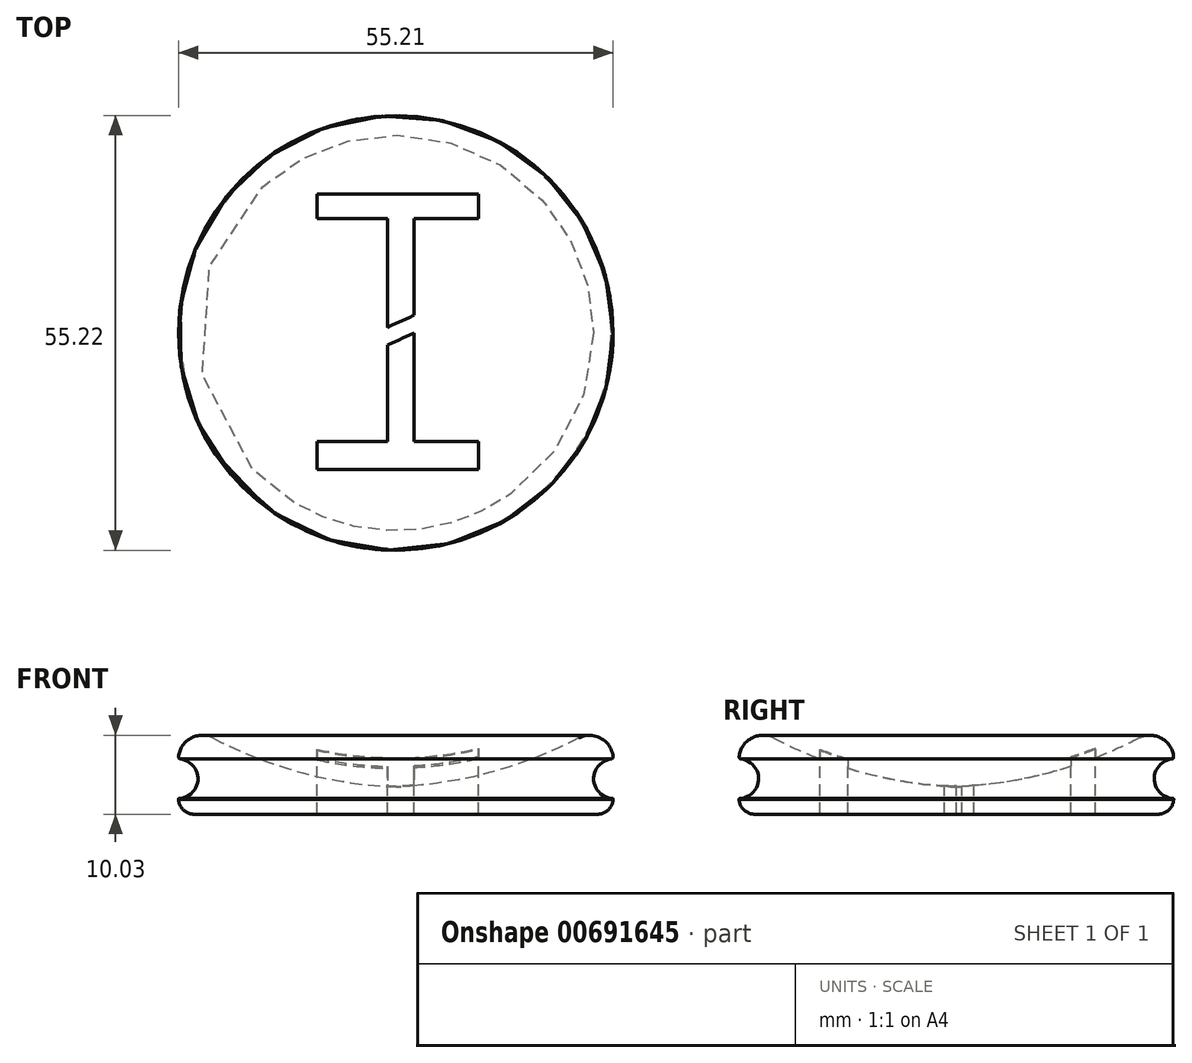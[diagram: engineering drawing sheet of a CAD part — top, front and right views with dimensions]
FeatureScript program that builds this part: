
annotation { "Feature Type Name" : "Feature", "Feature Type Description" : "" }
export const myFeature = defineFeature(function(context is Context, id is Id, definition is map)
    precondition{}
    {
        {
            var Q0;
            Q0=qCreatedBy(makeId("Front.planeOp"),FACE);
            var sketch = newSketch(context, id + "F0", { "sketchPlane" : qUnion([Q0])});
            skLineSegment(sketch, "E0.bottom", {"start": v(-25.5, -12.76) * mm, "end": v(-25, -12.76) * mm});
            skLineSegment(sketch, "E0.right", {"start": v(-25, -12.76) * mm, "end": v(-25, -2.76) * mm});
            skLineSegment(sketch, "E1.top", {"start": v(-25, -12.76) * mm, "end": v(0.1, -12.76) * mm});
            skLineSegment(sketch, "E1.left", {"start": v(-25, -2.76) * mm, "end": v(-25, -12.76) * mm});
            skPoint(sketch, "E2", {"position": v(0.1, -9.29) * mm});
            skArc(sketch, "E3", {"start": v(-23.1, -3.08) * mm, "mid": v(-12.17, -7.38) * mm, "end": v(-0.56, -9.26) * mm});
            skLineSegment(sketch, "E4", {"start": v(0.1, -12.76) * mm, "end": v(0.1, -9.76) * mm});
            skLineSegment(sketch, "E5", {"start": v(0.1, -0.79) * mm, "end": v(0.1, -9.29) * mm, "construction": true});
            skPoint(sketch, "E6.newPointB", {"position": v(-27.5, -2.76) * mm});
            skArc(sketch, "E6.filletArc", {"start": v(-23.1, -3.08) * mm, "mid": v(-25.93, -3.1) * mm, "end": v(-27.49, -5.46) * mm});
            skPoint(sketch, "E7.visualSharp", {"position": v(-27.5, -12.76) * mm});
            skArc(sketch, "E7.filletArc", {"start": v(-27.5, -10.85) * mm, "mid": v(-26.88, -12.2) * mm, "end": v(-25.5, -12.76) * mm});
            skArc(sketch, "E8", {"start": v(-27.41, -10.75) * mm, "mid": v(-25.02, -8.32) * mm, "end": v(-27.27, -5.75) * mm});
            skPoint(sketch, "E9", {"position": v(-27.27, -5.75) * mm});
            skPoint(sketch, "E10", {"position": v(-27.49, -5.46) * mm});
            skPoint(sketch, "E11", {"position": v(-27.5, -10.88) * mm});
            skPoint(sketch, "E12", {"position": v(-27.38, -10.75) * mm});
            skArc(sketch, "E13", {"start": v(-27.49, -5.46) * mm, "mid": v(-27.43, -5.64) * mm, "end": v(-27.27, -5.75) * mm});
            skArc(sketch, "E14", {"start": v(-27.41, -10.75) * mm, "mid": v(-27.47, -10.78) * mm, "end": v(-27.5, -10.85) * mm});
            skPoint(sketch, "E15", {"position": v(-0.56, -9.26) * mm});
            skPoint(sketch, "E16", {"position": v(0.1, -9.76) * mm});
            skLineSegment(sketch, "E17.trimOffspring", {"start": v(0.1, -9.76) * mm, "end": v(0.1, -18.73) * mm, "construction": true});
            skLineSegment(sketch, "E18", {"start": v(-0.56, -9.26) * mm, "end": v(0.1, -9.3) * mm});
            skLineSegment(sketch, "E19", {"start": v(0.1, -9.76) * mm, "end": v(0.1, -9.29) * mm});
            skSolve(sketch);
        }
        {
            var Q0;
            Q0 = qSketchRegion(id + "F0", true);
            var Q1;
            Q1 = qSketchRegion(id + "F22dS3yBFcY3S8e_1", true);
            var Q2;
            Q2=sQuery(id+"F0.wireOp",EDGE,"E5");
            revolve(context, id + "F1", {"entities" : qUnion([Q0, Q1]), "axis" : qUnion([Q2]), "revolveType" : RevolveType.FULL});
        }
        {
            var Q0;
            Q0=qCreatedBy(makeId("Top.planeOp"),FACE);
            var sketch = newSketch(context, id + "F2", { "sketchPlane" : qUnion([Q0])});
            skLineSegment(sketch, "E20", {"start": v(-0.95, -1.54) * mm, "end": v(2.44, 0) * mm});
            skLineSegment(sketch, "E21", {"start": v(2.44, 0) * mm, "end": v(2.44, -13.8) * mm});
            skLineSegment(sketch, "E22", {"start": v(2.44, -13.8) * mm, "end": v(10.6, -13.8) * mm});
            skLineSegment(sketch, "E23", {"start": v(10.6, -13.8) * mm, "end": v(10.6, -17.32) * mm});
            skLineSegment(sketch, "E24", {"start": v(-0.95, -1.54) * mm, "end": v(-0.95, -13.8) * mm});
            skLineSegment(sketch, "E25", {"start": v(-0.95, -13.8) * mm, "end": v(-9.87, -13.8) * mm});
            skLineSegment(sketch, "E26", {"start": v(-9.87, -13.8) * mm, "end": v(-9.87, -17.32) * mm});
            skLineSegment(sketch, "E27", {"start": v(10.6, -17.32) * mm, "end": v(-9.87, -17.32) * mm});
            skPoint(sketch, "E28.start.orphan", {"position": v(-2, 0) * mm});
            skLineSegment(sketch, "E29", {"start": v(-0.95, 1.56) * mm, "end": v(-0.95, 14.56) * mm});
            skLineSegment(sketch, "E30", {"start": v(-0.95, 14.56) * mm, "end": v(-9.87, 14.56) * mm});
            skLineSegment(sketch, "E31", {"start": v(2.44, 3.12) * mm, "end": v(2.44, 14.56) * mm});
            skLineSegment(sketch, "E32", {"start": v(2.44, 14.56) * mm, "end": v(10.6, 14.56) * mm});
            skLineSegment(sketch, "E33", {"start": v(10.6, 14.56) * mm, "end": v(10.6, 17.65) * mm});
            skLineSegment(sketch, "E34", {"start": v(10.6, 17.65) * mm, "end": v(-9.87, 17.65) * mm});
            skLineSegment(sketch, "E35", {"start": v(-9.87, 14.56) * mm, "end": v(-9.87, 17.65) * mm});
            skLineSegment(sketch, "E36", {"start": v(-0.95, 1.56) * mm, "end": v(-0.95, 0.72) * mm});
            skLineSegment(sketch, "E37", {"start": v(2.44, 3.12) * mm, "end": v(2.44, 2.26) * mm});
            skLineSegment(sketch, "E38", {"start": v(-0.95, 0.72) * mm, "end": v(2.44, 2.26) * mm});
            skSolve(sketch);
        }
        {
            var Q0;
            Q0=makeQuery(id+"F2.imprint","IMPRINT",FACE,{"disambiguationData":[TD([[makeQuery(id+"F2.imprint","IMPRINT",EDGE,{"derivedFrom":sQuery(id+"F2.wireOp",EDGE,"E20")}),-1.0]])]});
            var Q1;
            Q1=makeQuery(id+"F2.imprint","IMPRINT",FACE,{"disambiguationData":[TD([[makeQuery(id+"F2.imprint","IMPRINT",EDGE,{"derivedFrom":sQuery(id+"F2.wireOp",EDGE,"E29")}),-1.0]])]});
            extrude(context, id + "F3", {"entities" : qUnion([Q0, Q1]), "operationType" : NewBodyOperationType.REMOVE, "oppositeDirection" : true, "depth" : 25 * mm, "offsetDistance" : 25 * mm});
        }
    });
